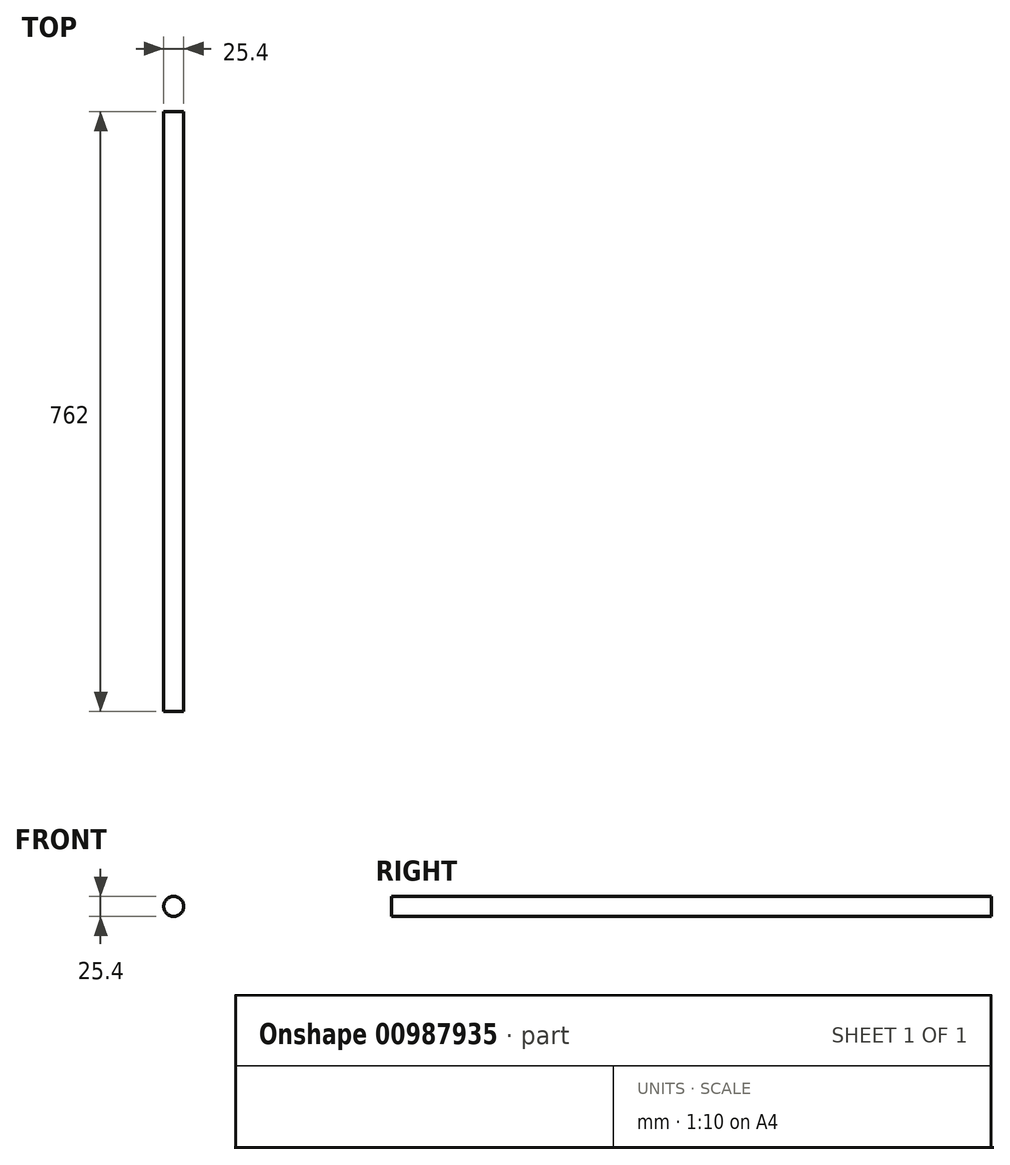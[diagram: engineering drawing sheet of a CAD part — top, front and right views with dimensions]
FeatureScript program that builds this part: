
annotation { "Feature Type Name" : "Feature", "Feature Type Description" : "" }
export const myFeature = defineFeature(function(context is Context, id is Id, definition is map)
    precondition{}
    {
        {
            var Q0;
            Q0=qCreatedBy(makeId("Front.planeOp"),FACE);
            var sketch = newSketch(context, id + "F0", { "sketchPlane" : qUnion([Q0])});
            skCircle(sketch, "E0", {"center": v(0, 0) * mm, "radius": 12.7 * mm});
            skSolve(sketch);
        }
        {
            var Q0;
            Q0=makeQuery(id+"F0.imprint","IMPRINT",FACE,{"disambiguationData":[TD([[makeQuery(id+"F0.imprint","IMPRINT",EDGE,{"derivedFrom":sQuery(id+"F0.wireOp",EDGE,"E0")}),1.0]])]});
            extrude(context, id + "F1", {"entities" : qUnion([Q0]), "depth" : 762 * mm, "offsetDistance" : 25.4 * mm});
        }
    });
